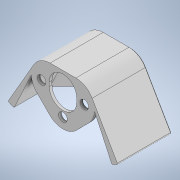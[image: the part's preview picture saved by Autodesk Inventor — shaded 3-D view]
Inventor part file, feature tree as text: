
AUTODESK INVENTOR PART (.ipt)
format: ipt  version: 2022.2 (Build 262287000, 287)  size: 323,072 bytes
history: native  units: mm
features: other x3, extrude x2, chamfer x2, sketch x2, projected_geometry x2, plane x1, split x1, draft x1, boolean_combine x1
ambient origin geometry x8: Origin, YZ Plane, XZ Plane, XY Plane, X Axis, Y Axis, Z Axis, Center Point
bodies: Solid2 (feature_tree), Solid1 (feature_tree), Solid3 (feature_tree), Solid4 (feature_tree)
feature tree (15):
  other  "Cover.ipt"
  extrude  "Extrusion1"  Depth=1.5mm
  extrude  "Extrusion2"  Depth=1.2mm
  plane  "Work Plane1"
  split  "Split1"
  draft  "FaceDraft1"
  chamfer  "Chamfer2"  Distance=0.6mm
  chamfer  "Chamfer3"  Distance=20.0mm
  boolean_combine  "Combine1"
  other  "Solid2::Cover.ipt"
  other  "TaggingFeature1"
  sketch  "Sketch1"  dims[d0=10.0mm d1=1.5mm]
  projected_geometry  "Projected Loop1"
  sketch  "Sketch2"  dims[d2=1.5mm d3=0.0mm d4=1.2mm d6=0.6mm d7=20.0mm d8=30.0deg d9=4.363323mm d10=28.0mm d11=1.5mm d12=0.0mm d13=0.0mm d14=-10.0mm d15=30.0deg d19=1.0mm d20=2.0mm d21=45.0deg d22=0.5mm d23=2.0mm d24=45.0deg]
  projected_geometry  "Projected Loop2"
